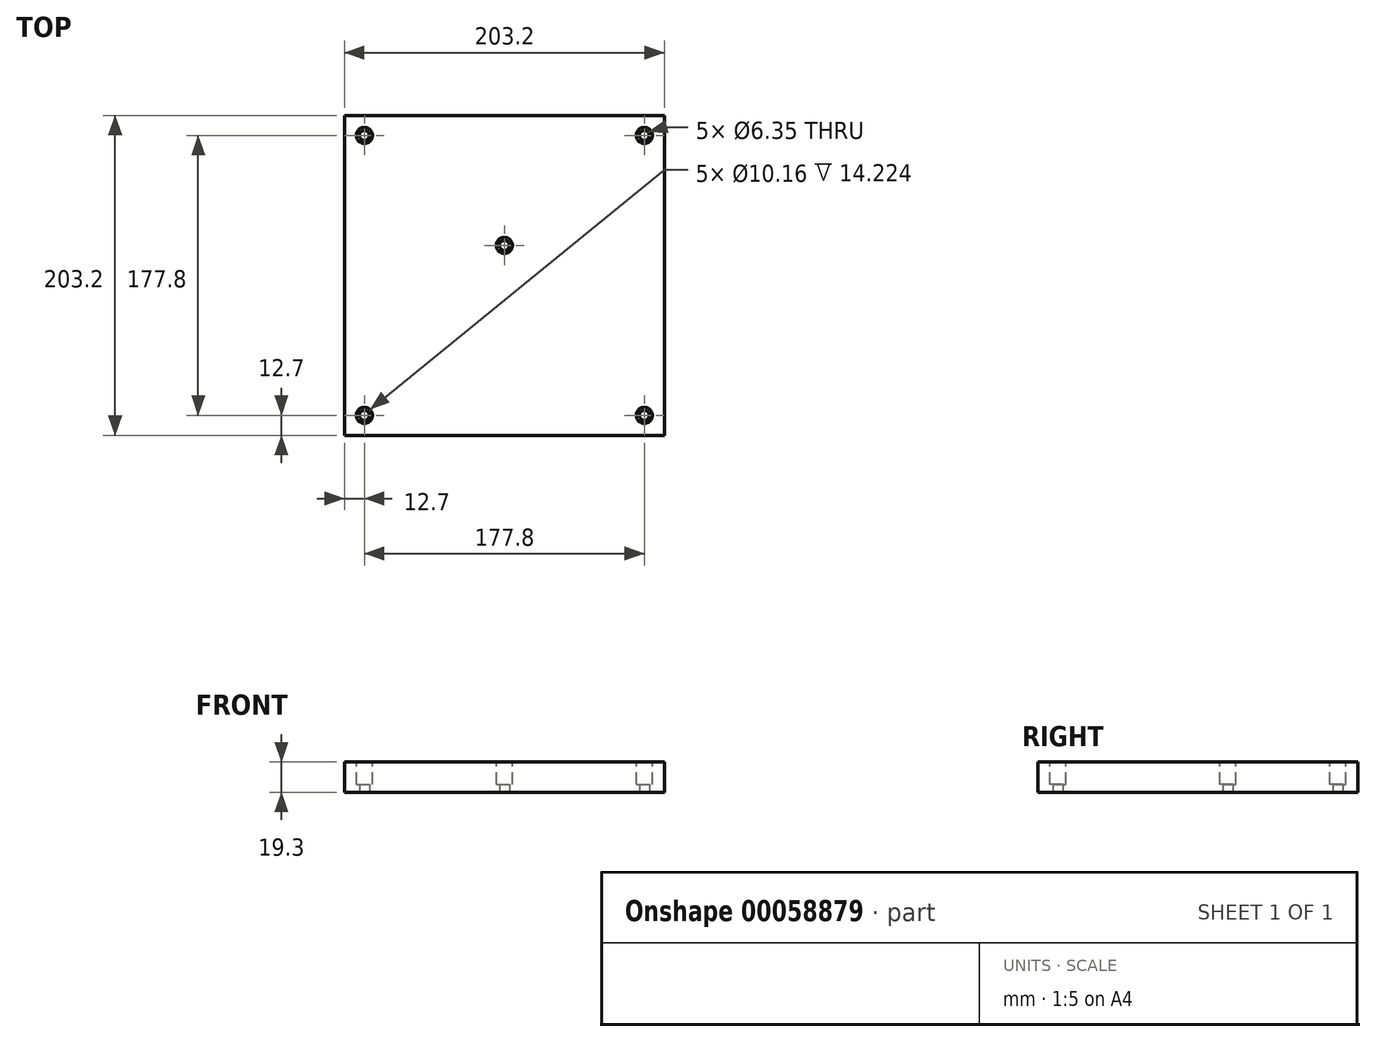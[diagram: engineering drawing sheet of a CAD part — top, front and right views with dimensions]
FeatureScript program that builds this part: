
annotation { "Feature Type Name" : "Feature", "Feature Type Description" : "" }
export const myFeature = defineFeature(function(context is Context, id is Id, definition is map)
    precondition{}
    {
        {
            var Q0;
            Q0=qCreatedBy(makeId("Top.planeOp"),FACE);
            var sketch = newSketch(context, id + "F0", { "sketchPlane" : qUnion([Q0])});
            skLineSegment(sketch, "E0.rect.bottom", {"start": v(101.6, -101.6) * mm, "end": v(-101.6, -101.6) * mm});
            skLineSegment(sketch, "E0.rect.top", {"start": v(101.6, 101.6) * mm, "end": v(-101.6, 101.6) * mm});
            skLineSegment(sketch, "E0.rect.left", {"start": v(101.6, -101.6) * mm, "end": v(101.6, 101.6) * mm});
            skLineSegment(sketch, "E0.rect.right", {"start": v(-101.6, -101.6) * mm, "end": v(-101.6, 101.6) * mm});
            skPoint(sketch, "E0.rect.middle", {"position": v(0, 0) * mm});
            skCircle(sketch, "E1", {"center": v(88.9, 88.9) * mm, "radius": 3.18 * mm});
            skCircle(sketch, "E2", {"center": v(-88.9, 88.9) * mm, "radius": 3.18 * mm});
            skCircle(sketch, "E3", {"center": v(-88.9, -88.9) * mm, "radius": 3.18 * mm});
            skCircle(sketch, "E4", {"center": v(88.9, -88.9) * mm, "radius": 3.18 * mm});
            skLineSegment(sketch, "E5.rect.bottom", {"start": v(88.9, 88.9) * mm, "end": v(-88.9, 88.9) * mm, "construction": true});
            skLineSegment(sketch, "E5.rect.top", {"start": v(88.9, -88.9) * mm, "end": v(-88.9, -88.9) * mm, "construction": true});
            skLineSegment(sketch, "E5.rect.left", {"start": v(88.9, 88.9) * mm, "end": v(88.9, -88.9) * mm, "construction": true});
            skLineSegment(sketch, "E5.rect.right", {"start": v(-88.9, 88.9) * mm, "end": v(-88.9, -88.9) * mm, "construction": true});
            skCircle(sketch, "E6", {"center": v(0, 19.05) * mm, "radius": 3.18 * mm});
            skSolve(sketch);
        }
        {
            var Q0;
            Q0=qSketchRegion(id+"F0",true);
            extrude(context, id + "F1", {"entities" : qUnion([Q0]), "depth" : 19.3 * mm});
        }
        {
            var Q0;
            Q0=makeQuery(id+"F1.opExtrude","CAP_FACE",FACE,{"disambiguationData":[OSD([sQuery(id+"F0.wireOp",EDGE,"E0.rect.bottom"),sQuery(id+"F0.wireOp",EDGE,"E0.rect.top"),sQuery(id+"F0.wireOp",EDGE,"E0.rect.left"),sQuery(id+"F0.wireOp",EDGE,"E0.rect.right"),sQuery(id+"F0.wireOp",EDGE,"E1"),sQuery(id+"F0.wireOp",EDGE,"E2"),sQuery(id+"F0.wireOp",EDGE,"E3"),sQuery(id+"F0.wireOp",EDGE,"E4"),sQuery(id+"F0.wireOp",EDGE,"E6")])],"isStart":false});
            var sketch = newSketch(context, id + "F2", { "sketchPlane" : qUnion([Q0])});
            skCircle(sketch, "E7", {"center": v(-88.9, 88.9) * mm, "radius": 5.08 * mm});
            skCircle(sketch, "E8", {"center": v(0, 19.05) * mm, "radius": 5.08 * mm});
            skCircle(sketch, "E9", {"center": v(88.9, 88.9) * mm, "radius": 5.08 * mm});
            skCircle(sketch, "E10", {"center": v(-88.9, -88.9) * mm, "radius": 5.08 * mm});
            skCircle(sketch, "E11", {"center": v(88.9, -88.9) * mm, "radius": 5.08 * mm});
            skSolve(sketch);
        }
        {
            var Q0;
            Q0=makeQuery(id+"F1.opExtrude","CAP_FACE",FACE,{"disambiguationData":[OSD([sQuery(id+"F0.wireOp",EDGE,"E0.rect.bottom"),sQuery(id+"F0.wireOp",EDGE,"E0.rect.top"),sQuery(id+"F0.wireOp",EDGE,"E0.rect.left"),sQuery(id+"F0.wireOp",EDGE,"E0.rect.right"),sQuery(id+"F0.wireOp",EDGE,"E1"),sQuery(id+"F0.wireOp",EDGE,"E2"),sQuery(id+"F0.wireOp",EDGE,"E3"),sQuery(id+"F0.wireOp",EDGE,"E4"),sQuery(id+"F0.wireOp",EDGE,"E6")])],"isStart":true});
            cPlane(context, id + "F3", {"entities" : qUnion([Q0]), "cplaneType" : CPlaneType.OFFSET, "offset" : 5.08 * mm, "oppositeDirection" : true, "width" : 152.4 * mm, "height" : 152.4 * mm});
        }
        {
            var Q0;
            Q0=qSketchRegion(id+"F2",true);
            var Q1;
            Q1=qCreatedBy(id+"F3.planeOp",FACE);
            extrude(context, id + "F4", {"entities" : qUnion([Q0]), "operationType" : NewBodyOperationType.REMOVE, "endBound" : BoundingType.UP_TO_SURFACE, "oppositeDirection" : true, "endBoundEntityFace" : qUnion([Q1]), "depth" : 25.4 * mm});
        }
    });
